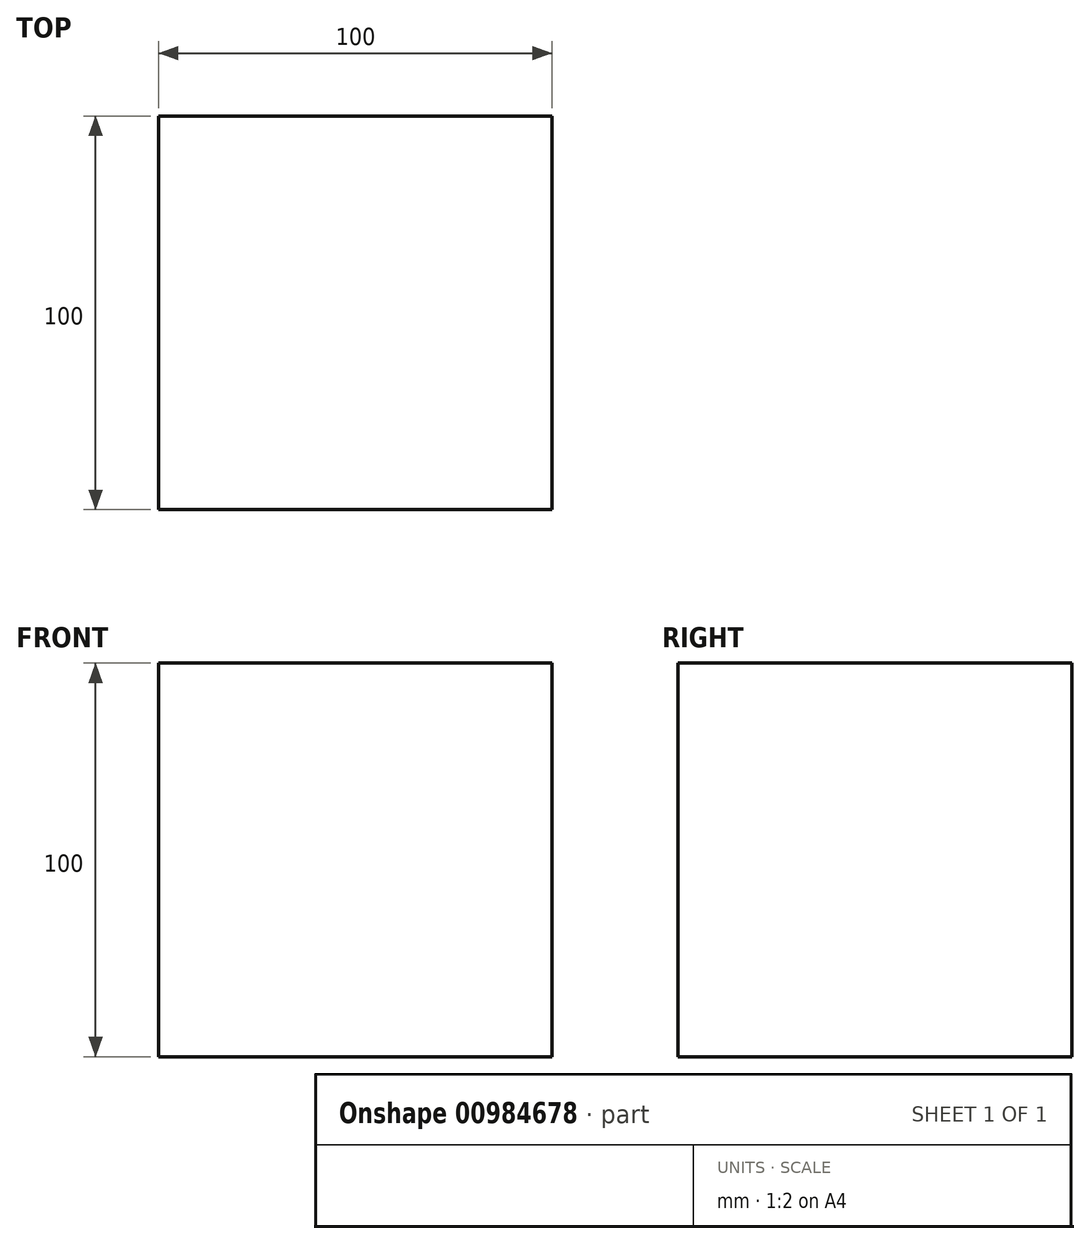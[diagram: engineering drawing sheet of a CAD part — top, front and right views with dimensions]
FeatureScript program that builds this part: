
annotation { "Feature Type Name" : "Feature", "Feature Type Description" : "" }
export const myFeature = defineFeature(function(context is Context, id is Id, definition is map)
    precondition{}
    {
        {
            var Q0;
            Q0=qCreatedBy(makeId("Front.planeOp"),FACE);
            var sketch = newSketch(context, id + "F0", { "sketchPlane" : qUnion([Q0])});
            skLineSegment(sketch, "E0.bottom", {"start": v(-49.29, 67.39) * mm, "end": v(50.71, 67.39) * mm});
            skLineSegment(sketch, "E0.top", {"start": v(-49.29, -32.61) * mm, "end": v(50.71, -32.61) * mm});
            skLineSegment(sketch, "E0.left", {"start": v(-49.29, 67.39) * mm, "end": v(-49.29, -32.61) * mm});
            skLineSegment(sketch, "E0.right", {"start": v(50.71, 67.39) * mm, "end": v(50.71, -32.61) * mm});
            skSolve(sketch);
        }
        {
            var Q0;
            Q0=makeQuery(id+"F0.imprint","IMPRINT",FACE,{"disambiguationData":[TD([[makeQuery(id+"F0.imprint","IMPRINT",EDGE,{"derivedFrom":sQuery(id+"F0.wireOp",EDGE,"E0.bottom")}),-1.0]])]});
            extrude(context, id + "F1", {"entities" : qUnion([Q0]), "oppositeDirection" : true, "depth" : 100 * mm, "offsetDistance" : 25 * mm});
        }
    });
